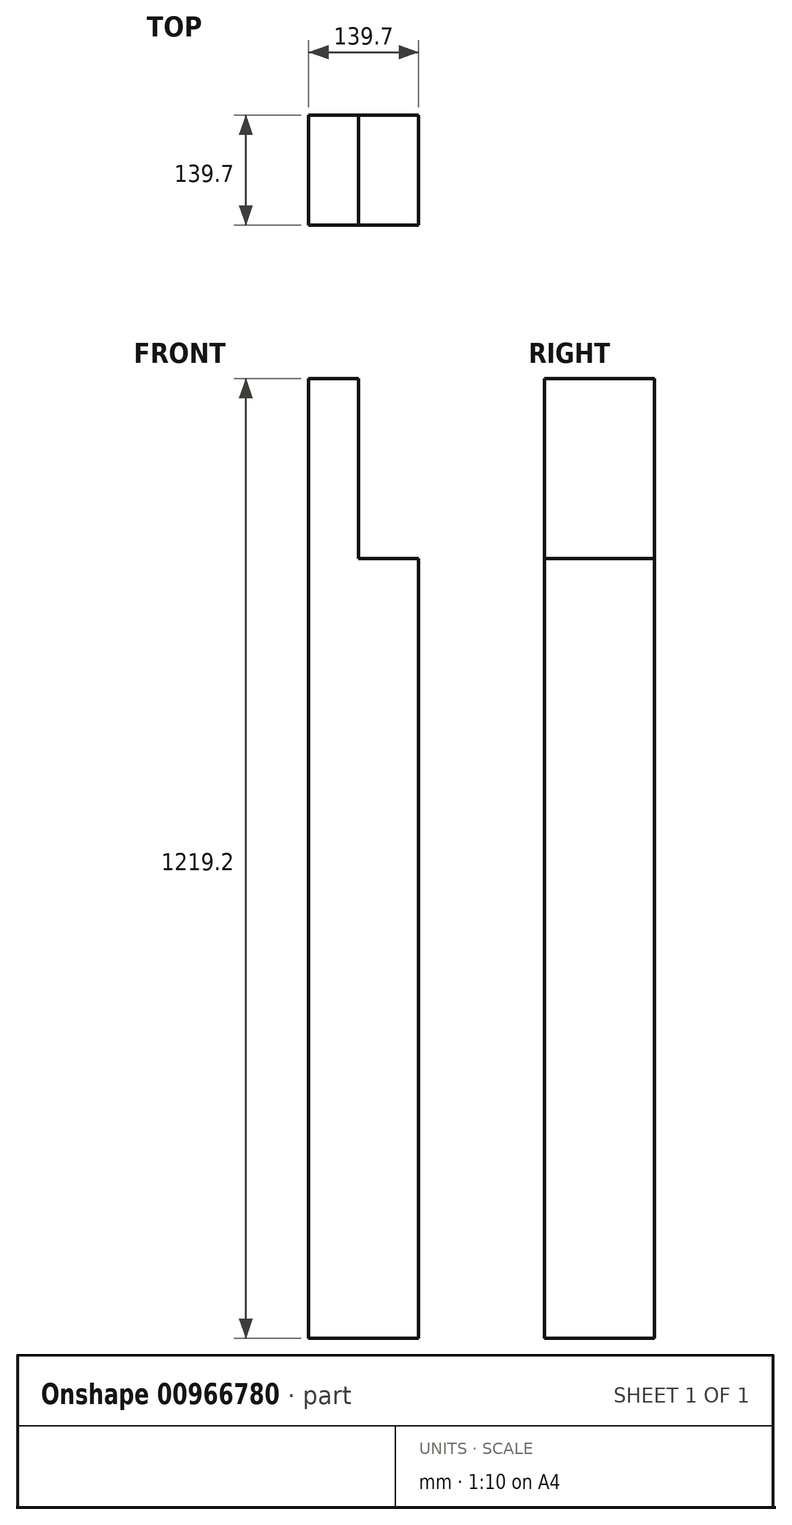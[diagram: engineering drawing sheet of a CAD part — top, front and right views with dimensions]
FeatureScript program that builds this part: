
annotation { "Feature Type Name" : "Feature", "Feature Type Description" : "" }
export const myFeature = defineFeature(function(context is Context, id is Id, definition is map)
    precondition{}
    {
        {
            var Q0;
            Q0=qCreatedBy(makeId("Front.planeOp"),FACE);
            var sketch = newSketch(context, id + "F0", { "sketchPlane" : qUnion([Q0])});
            skLineSegment(sketch, "E0", {"start": v(0, 0) * mm, "end": v(0, 1219.2) * mm});
            skLineSegment(sketch, "E1", {"start": v(0, 1219.2) * mm, "end": v(63.5, 1219.2) * mm});
            skLineSegment(sketch, "E2", {"start": v(63.5, 1219.2) * mm, "end": v(63.5, 990.6) * mm});
            skLineSegment(sketch, "E3", {"start": v(63.5, 990.6) * mm, "end": v(139.7, 990.6) * mm});
            skLineSegment(sketch, "E4", {"start": v(139.7, 990.6) * mm, "end": v(139.7, 0) * mm});
            skLineSegment(sketch, "E5", {"start": v(139.7, 0) * mm, "end": v(0, 0) * mm});
            skSolve(sketch);
        }
        {
            var Q0;
            Q0=makeQuery(id+"F0.imprint","IMPRINT",FACE,{"disambiguationData":[TD([[makeQuery(id+"F0.imprint","IMPRINT",EDGE,{"derivedFrom":sQuery(id+"F0.wireOp",EDGE,"E0")}),-1.0]])]});
            extrude(context, id + "F1", {"entities" : qUnion([Q0]), "depth" : 139.7 * mm, "offsetDistance" : 25.4 * mm});
        }
    });
